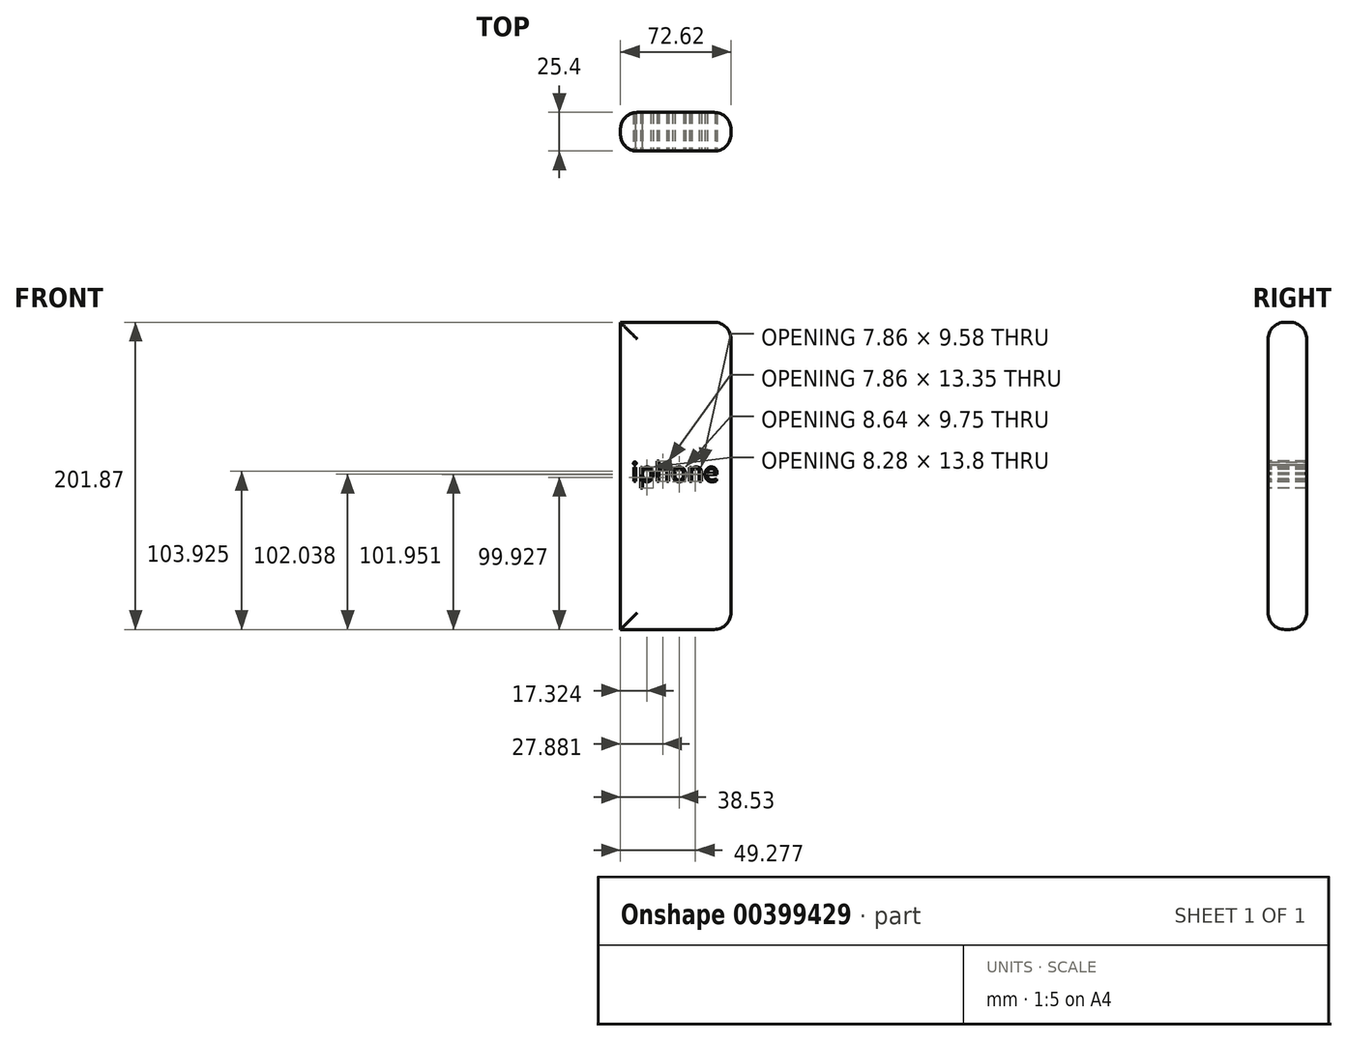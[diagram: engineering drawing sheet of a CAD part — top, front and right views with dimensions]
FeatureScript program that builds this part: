
annotation { "Feature Type Name" : "Feature", "Feature Type Description" : "" }
export const myFeature = defineFeature(function(context is Context, id is Id, definition is map)
    precondition{}
    {
        {
            var Q0;
            Q0=qCreatedBy(makeId("Front.planeOp"),FACE);
            var sketch = newSketch(context, id + "F0", { "sketchPlane" : qUnion([Q0])});
            skLineSegment(sketch, "E0.bottom", {"start": v(-21.7, 81.52) * mm, "end": v(50.9, 81.52) * mm});
            skLineSegment(sketch, "E0.top", {"start": v(-21.7, -120.35) * mm, "end": v(50.9, -120.35) * mm});
            skLineSegment(sketch, "E0.left", {"start": v(-21.7, 81.52) * mm, "end": v(-21.7, -120.35) * mm});
            skLineSegment(sketch, "E0.right", {"start": v(50.9, 81.52) * mm, "end": v(50.9, -120.35) * mm});
            skSolve(sketch);
        }
        {
            var Q0;
            Q0 = qSketchRegion(id + "F0", true);
            extrude(context, id + "F1", {"entities" : qUnion([Q0]), "depth" : 25.4 * mm});
        }
        {
            var Q0;
            Q0=makeQuery(id+"F1.opExtrude","CAP_EDGE",EDGE,{"disambiguationData":[OSD([sQuery(id+"F0.wireOp",EDGE,"E0.bottom")])],"isStart":false});
            var Q1;
            Q1=makeQuery(id+"F1.opExtrude","CAP_EDGE",EDGE,{"disambiguationData":[OSD([sQuery(id+"F0.wireOp",EDGE,"E0.bottom")])],"isStart":true});
            var Q2;
            Q2=makeQuery(id+"F1.opExtrude","CAP_EDGE",EDGE,{"disambiguationData":[OSD([sQuery(id+"F0.wireOp",EDGE,"E0.right")])],"isStart":false});
            var Q3;
            Q3=makeQuery(id+"F1.opExtrude","SWEPT_FACE",FACE,{"disambiguationData":[OSD([sQuery(id+"F0.wireOp",EDGE,"E0.right")])]});
            var Q4;
            Q4=makeQuery(id+"F1.opExtrude","CAP_EDGE",EDGE,{"disambiguationData":[OSD([sQuery(id+"F0.wireOp",EDGE,"E0.left")])],"isStart":false});
            var Q5;
            Q5=makeQuery(id+"F1.opExtrude","CAP_FACE",FACE,{"disambiguationData":[OSD([sQuery(id+"F0.wireOp",EDGE,"E0.bottom"),sQuery(id+"F0.wireOp",EDGE,"E0.top"),sQuery(id+"F0.wireOp",EDGE,"E0.left"),sQuery(id+"F0.wireOp",EDGE,"E0.right")])],"isStart":true});
            var Q6;
            Q6=makeQuery(id+"F1.opExtrude","CAP_EDGE",EDGE,{"disambiguationData":[OSD([sQuery(id+"F0.wireOp",EDGE,"E0.top")])],"isStart":false});
            fillet(context, id + "F2", {"entities" : qUnion([Q0, Q1, Q2, Q3, Q4, Q5, Q6]), "radius" : 11.04 * mm, "tangentPropagation" : true, "allowEdgeOverflow" : false});
        }
        {
            var Q0;
            Q0=makeQuery(id+"F1.opExtrude","CAP_FACE",FACE,{"disambiguationData":[OSD([sQuery(id+"F0.wireOp",EDGE,"E0.bottom"),sQuery(id+"F0.wireOp",EDGE,"E0.top"),sQuery(id+"F0.wireOp",EDGE,"E0.left"),sQuery(id+"F0.wireOp",EDGE,"E0.right")])],"isStart":false});
            var sketch = newSketch(context, id + "F3", { "sketchPlane" : qUnion([Q0])});
            skText(sketch, "E1", { "text": "iphone", "fontName": "OpenSans-Regular.ttf"});
            const initialGuessF3  = {"E1": [-0.01448, -0.0231, 1, 0, 0.01265]};
            skSetInitialGuess(sketch, initialGuessF3);
            skSolve(sketch);
        }
        {
            var Q0;
            Q0 = qSketchRegion(id + "F3", true);
            extrude(context, id + "F4", {"entities" : qUnion([Q0]), "operationType" : NewBodyOperationType.REMOVE, "oppositeDirection" : true, "depth" : 37.34 * mm});
        }
    });
